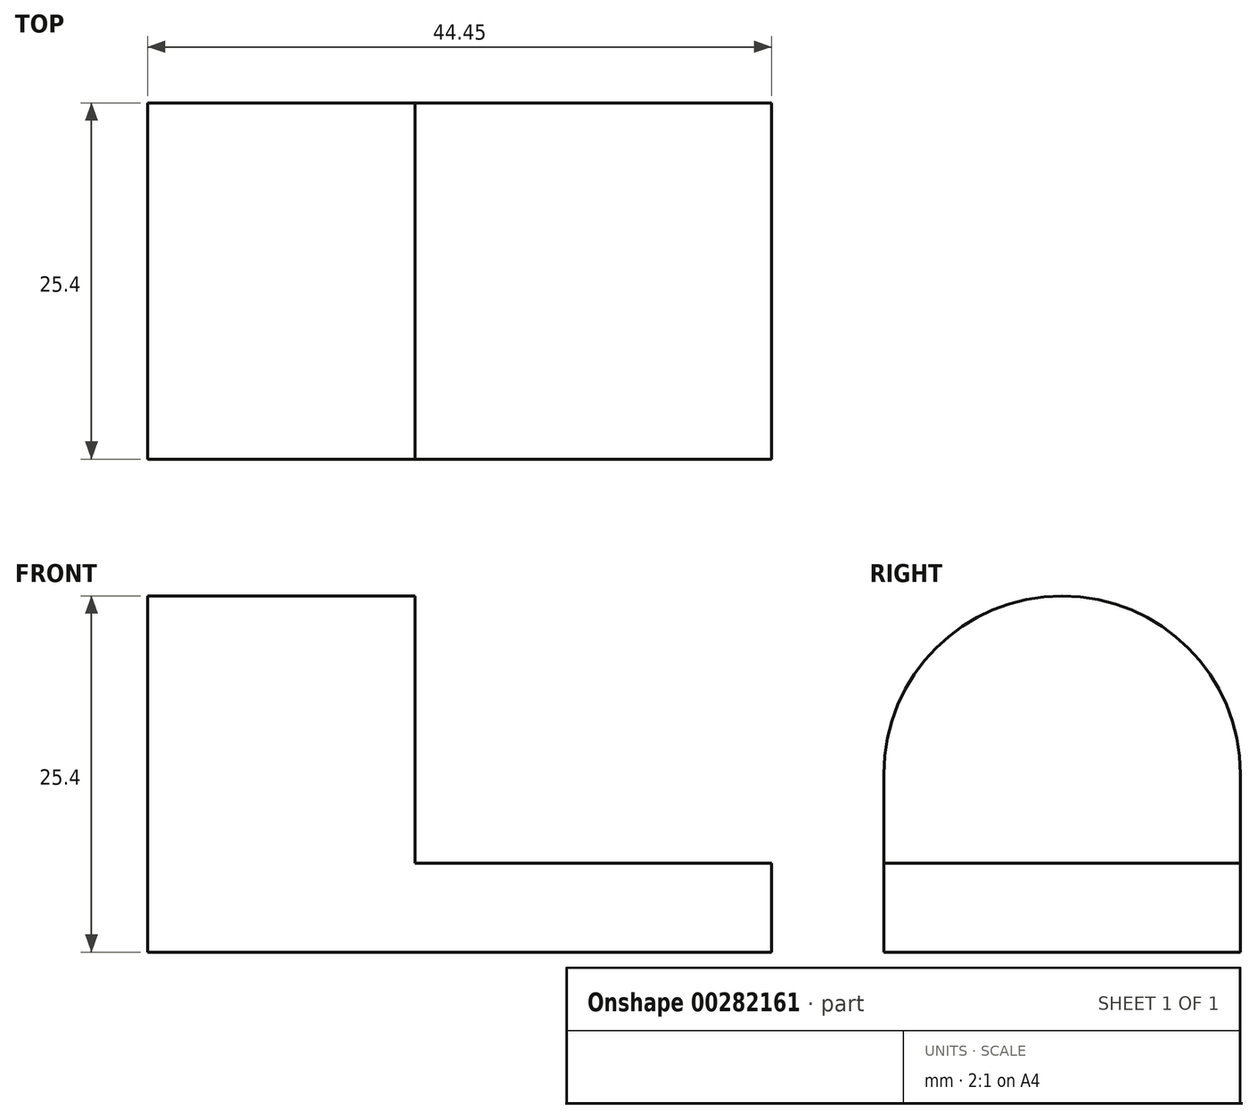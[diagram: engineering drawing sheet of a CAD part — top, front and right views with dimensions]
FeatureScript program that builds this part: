
annotation { "Feature Type Name" : "Feature", "Feature Type Description" : "" }
export const myFeature = defineFeature(function(context is Context, id is Id, definition is map)
    precondition{}
    {
        {
            var Q0;
            Q0=qCreatedBy(makeId("Front.planeOp"),FACE);
            var sketch = newSketch(context, id + "F0", { "sketchPlane" : qUnion([Q0])});
            skLineSegment(sketch, "E0", {"start": v(0, 0) * mm, "end": v(0, 12.7) * mm});
            skLineSegment(sketch, "E1", {"start": v(0, 12.7) * mm, "end": v(19.05, 12.7) * mm});
            skLineSegment(sketch, "E2", {"start": v(19.05, 12.7) * mm, "end": v(19.05, 6.35) * mm});
            skLineSegment(sketch, "E3", {"start": v(19.05, 6.35) * mm, "end": v(44.45, 6.35) * mm});
            skLineSegment(sketch, "E4", {"start": v(44.45, 6.35) * mm, "end": v(44.45, 0) * mm});
            skLineSegment(sketch, "E5", {"start": v(44.45, 0) * mm, "end": v(0, 0) * mm});
            skSolve(sketch);
        }
        {
            var Q0;
            Q0=makeQuery(id+"F0.imprint","IMPRINT",FACE,{"disambiguationData":[TD([[makeQuery(id+"F0.imprint","IMPRINT",EDGE,{"derivedFrom":sQuery(id+"F0.wireOp",EDGE,"E0")}),-1.0]])]});
            extrude(context, id + "F1", {"entities" : qUnion([Q0]), "depth" : 25.4 * mm});
        }
        {
            var Q0;
            Q0=makeQuery(id+"F1.opExtrude","SWEPT_FACE",FACE,{"disambiguationData":[OSD([sQuery(id+"F0.wireOp",EDGE,"E2")])]});
            var sketch = newSketch(context, id + "F2", { "sketchPlane" : qUnion([Q0])});
            skArc(sketch, "E6", {"start": v(0, 12.7) * mm, "mid": v(-12.7, 25.4) * mm, "end": v(-25.4, 12.7) * mm});
            skSolve(sketch);
        }
        {
            var Q0;
            Q0=makeQuery(id+"F2.imprint","IMPRINT",FACE,{"disambiguationData":[TD([[makeQuery(id+"F2.imprint","IMPRINT",EDGE,{"derivedFrom":sQuery(id+"F2.wireOp",EDGE,"E6")}),1.0]])]});
            var Q1;
            Q1=makeQuery(id+"F1.opExtrude","SWEPT_FACE",FACE,{"disambiguationData":[OSD([sQuery(id+"F0.wireOp",EDGE,"E0")])]});
            extrude(context, id + "F3", {"entities" : qUnion([Q0]), "operationType" : NewBodyOperationType.ADD, "endBound" : BoundingType.UP_TO_SURFACE, "oppositeDirection" : true, "endBoundEntityFace" : qUnion([Q1]), "depth" : 25.4 * mm});
        }
    });
